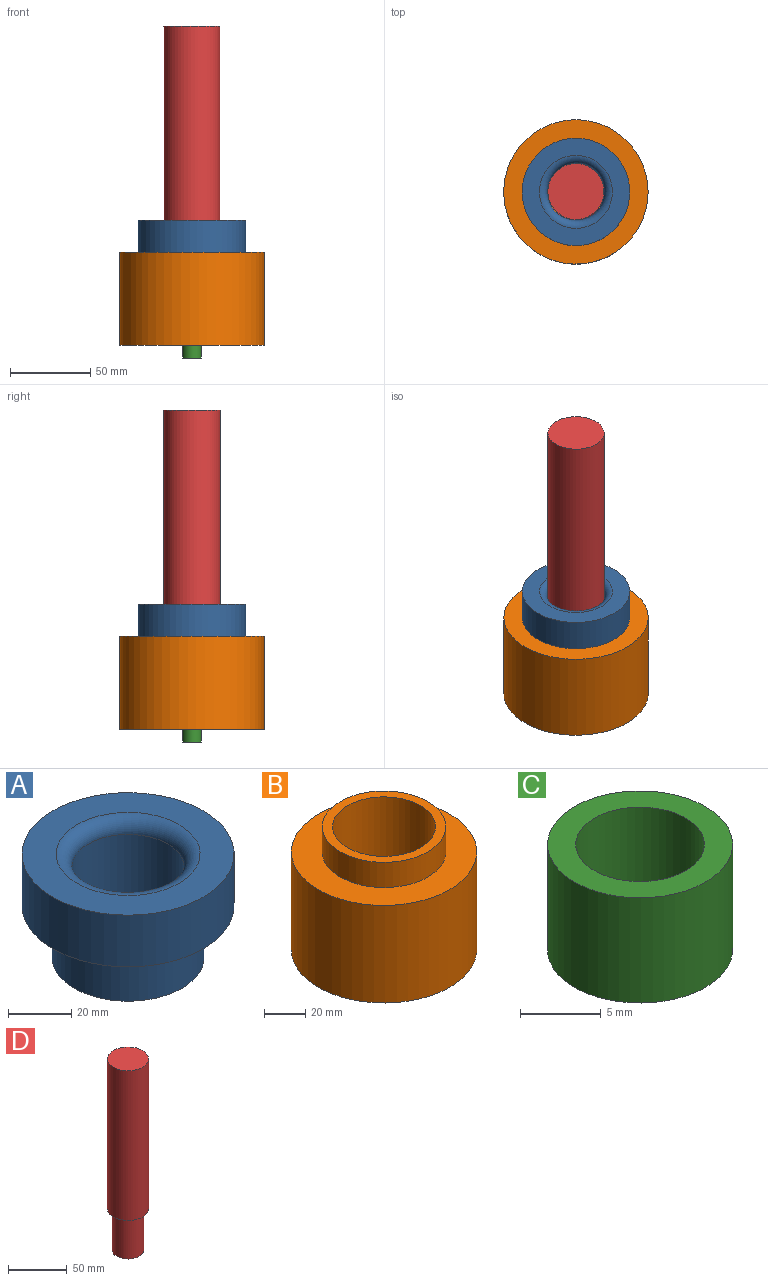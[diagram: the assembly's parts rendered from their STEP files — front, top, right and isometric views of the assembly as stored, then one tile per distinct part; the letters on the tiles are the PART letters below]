
ASSEMBLY  parts=4 mates=3
PART A: 9 faces, bbox 67x67x40 mm
  f0: cylinder r=17.75mm len=35.5mm, axis (0,0,-1), area 3903.4mm2, adj f6,f8
  f1: cylinder r=24mm len=48mm, axis (0,0,-1), area 3769.9mm2, adj f2,f6
  f2: plane 60x60mm, normal (0,0,-1), area 1017.9mm2, adj f1,f3
  f3: cylinder r=30mm len=60mm, axis (0,0,1), area 942.5mm2, adj f2,f5
  f4: cylinder r=33.5mm len=67mm, axis (0,0,1), area 4209.7mm2, adj f5,f7
  f5: plane 67x67mm, normal (0,0,-1), area 698.2mm2, adj f3,f4
  f6: plane 48x48mm, normal (0,0,-1), area 819.8mm2, adj f0,f1
  f7: plane 67x67mm, normal (0,0,1), area 1899.7mm2, adj f4,f8
  f8: torus R=22.75mm, axis (0,0,1), area 965.6mm2, adj f0,f7
PART B: 8 faces, bbox 90x90x73 mm
  f0: cylinder r=45mm len=90mm, axis (0,0,-1), area 16399.1mm2, adj f4,f7
  f1: plane 60x60mm, normal (0,0,1), area 863.9mm2, adj f5,f6
  f2: cylinder r=15.5mm len=31mm, axis (0,0,-1), area 194.8mm2, adj f3,f4
  f3: plane 50x50mm, normal (0,0,1), area 1208.7mm2, adj f2,f5
  f4: plane 90x90mm, normal (0,0,-1), area 5607mm2, adj f0,f2
  f5: cylinder r=25mm len=71mm, axis (0,0,-1), area 11152.7mm2, adj f1,f3
  f6: cylinder r=30mm len=60mm, axis (0,0,1), area 2827.4mm2, adj f1,f7
  f7: plane 90x90mm, normal (0,0,1), area 3534.3mm2, adj f0,f6
PART C: 5 faces, bbox 11.5x11.5x8 mm
  f0: cylinder r=5.75mm len=11.5mm, axis (0,0,-1), area 289mm2, adj f1,f2
  f1: plane 11.5x11.5mm, normal (0,0,1), area 53.6mm2, adj f0,f3
  f2: plane 11.5x11.5mm, normal (0,0,-1), area 103.9mm2, adj f0
  f3: cylinder r=4mm len=8mm, axis (0,0,1), area 175.9mm2, adj f1,f4
  f4: plane 8x8mm, normal (0,0,1), area 50.3mm2, adj f3
PART D: 5 faces, bbox 35x35x199 mm
  f0: cylinder r=13.5mm len=43mm, axis (0,0,-1), area 3647.4mm2, adj f1,f4
  f1: plane 27x27mm, normal (0,0,-1), area 572.6mm2, adj f0
  f2: cylinder r=17.5mm len=156mm, axis (0,0,-1), area 17153.1mm2, adj f3,f4
  f3: plane 35x35mm, normal (0,0,1), area 962.1mm2, adj f2
  f4: plane 35x35mm, normal (0,0,-1), area 389.6mm2, adj f0,f2
PLACE A t=(-17.76,3.92,-7.24)mm
PLACE B t=(-17.76,3.92,-15.24)mm
PLACE C rot(axis=(0,1,0),180deg) t=(-17.76,3.92,-15.24)mm
PLACE D t=(-17.76,3.92,-15.24)mm
MATE fastened D.f0 <-> B.f0  axis (0,0,-1) through (-17.76,3.92,-15.24)mm
MATE fastened A.f0 <-> B.f5  axis (0,0,-1) through (-17.76,3.92,57.76)mm
MATE fastened C.f0 <-> D.f0  axis (0,0,1) through (-17.76,3.92,-15.24)mm
